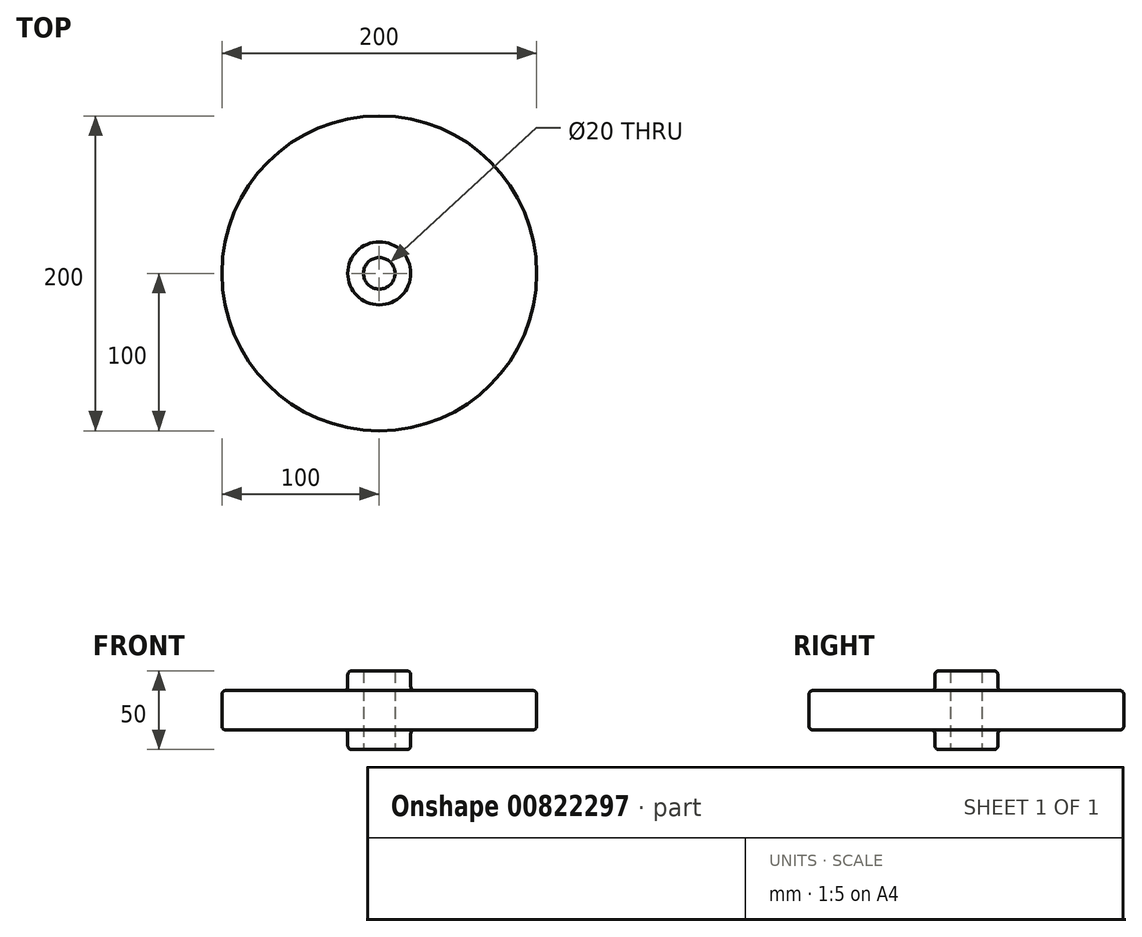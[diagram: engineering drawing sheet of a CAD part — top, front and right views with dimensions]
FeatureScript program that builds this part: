
annotation { "Feature Type Name" : "Feature", "Feature Type Description" : "" }
export const myFeature = defineFeature(function(context is Context, id is Id, definition is map)
    precondition{}
    {
        {
            var Q0;
            Q0=qCreatedBy(makeId("Top.planeOp"),FACE);
            var sketch = newSketch(context, id + "F0", { "sketchPlane" : qUnion([Q0])});
            skCircle(sketch, "E0", {"center": v(0, 0) * mm, "radius": 100 * mm});
            skCircle(sketch, "E1", {"center": v(0, 0) * mm, "radius": 10 * mm});
            skSolve(sketch);
        }
        {
            var Q0;
            Q0=makeQuery(id+"F0.imprint","IMPRINT",FACE,{"disambiguationData":[TD([[makeQuery(id+"F0.imprint","IMPRINT",EDGE,{"derivedFrom":sQuery(id+"F0.wireOp",EDGE,"E0")}),1.0]])]});
            extrude(context, id + "F1", {"entities" : qUnion([Q0]), "depth" : 25 * mm, "offsetDistance" : 25 * mm});
        }
        {
            var Q0;
            Q0=makeQuery(id+"F1.opExtrude","CAP_FACE",FACE,{"disambiguationData":[OSD([sQuery(id+"F0.wireOp",EDGE,"E0"),sQuery(id+"F0.wireOp",EDGE,"E1")])],"isStart":false});
            var sketch = newSketch(context, id + "F2", { "sketchPlane" : qUnion([Q0])});
            skCircle(sketch, "E2", {"center": v(0, 0) * mm, "radius": 20 * mm});
            skCircle(sketch, "E3", {"center": v(0, 0) * mm, "radius": 10 * mm});
            skSolve(sketch);
        }
        {
            var Q0;
            Q0 = qSketchRegion(id + "F2", true);
            extrude(context, id + "F3", {"entities" : qUnion([Q0]), "operationType" : NewBodyOperationType.ADD, "depth" : 12.5 * mm, "offsetDistance" : 25 * mm});
        }
        {
            var Q0;
            Q0=makeQuery(id+"F1.opExtrude","CAP_FACE",FACE,{"disambiguationData":[OSD([sQuery(id+"F0.wireOp",EDGE,"E0"),sQuery(id+"F0.wireOp",EDGE,"E1")])],"isStart":true});
            var sketch = newSketch(context, id + "F4", { "sketchPlane" : qUnion([Q0])});
            skCircle(sketch, "E4", {"center": v(0, 0) * mm, "radius": 10 * mm});
            skCircle(sketch, "E5", {"center": v(0, 0) * mm, "radius": 20 * mm});
            skSolve(sketch);
        }
        {
            var Q0;
            Q0 = qSketchRegion(id + "F4", true);
            extrude(context, id + "F5", {"entities" : qUnion([Q0]), "operationType" : NewBodyOperationType.ADD, "depth" : 12.5 * mm, "offsetDistance" : 25 * mm});
        }
        {
            var Q0;
            Q0=makeQuery(id+"F1.opExtrude","CAP_FACE",FACE,{"disambiguationData":[OSD([sQuery(id+"F0.wireOp",EDGE,"E0"),sQuery(id+"F0.wireOp",EDGE,"E1")])],"isStart":true});
            var Q1;
            Q1=makeQuery(id+"F1.opExtrude","CAP_FACE",FACE,{"disambiguationData":[OSD([sQuery(id+"F0.wireOp",EDGE,"E0"),sQuery(id+"F0.wireOp",EDGE,"E1")])],"isStart":false});
            var Q2;
            Q2=makeQuery(id+"F5.opExtrude","CAP_EDGE",EDGE,{"disambiguationData":[OSD([sQuery(id+"F4.wireOp",EDGE,"E5")])],"isStart":false});
            var Q3;
            Q3=makeQuery(id+"F3.opExtrude","CAP_EDGE",EDGE,{"disambiguationData":[OSD([sQuery(id+"F2.wireOp",EDGE,"E2")])],"isStart":false});
            fillet(context, id + "F6", {"entities" : qUnion([Q0, Q1, Q2, Q3]), "radius" : 2.5 * mm, "tangentPropagation" : true, "allowEdgeOverflow" : false});
        }
    });
